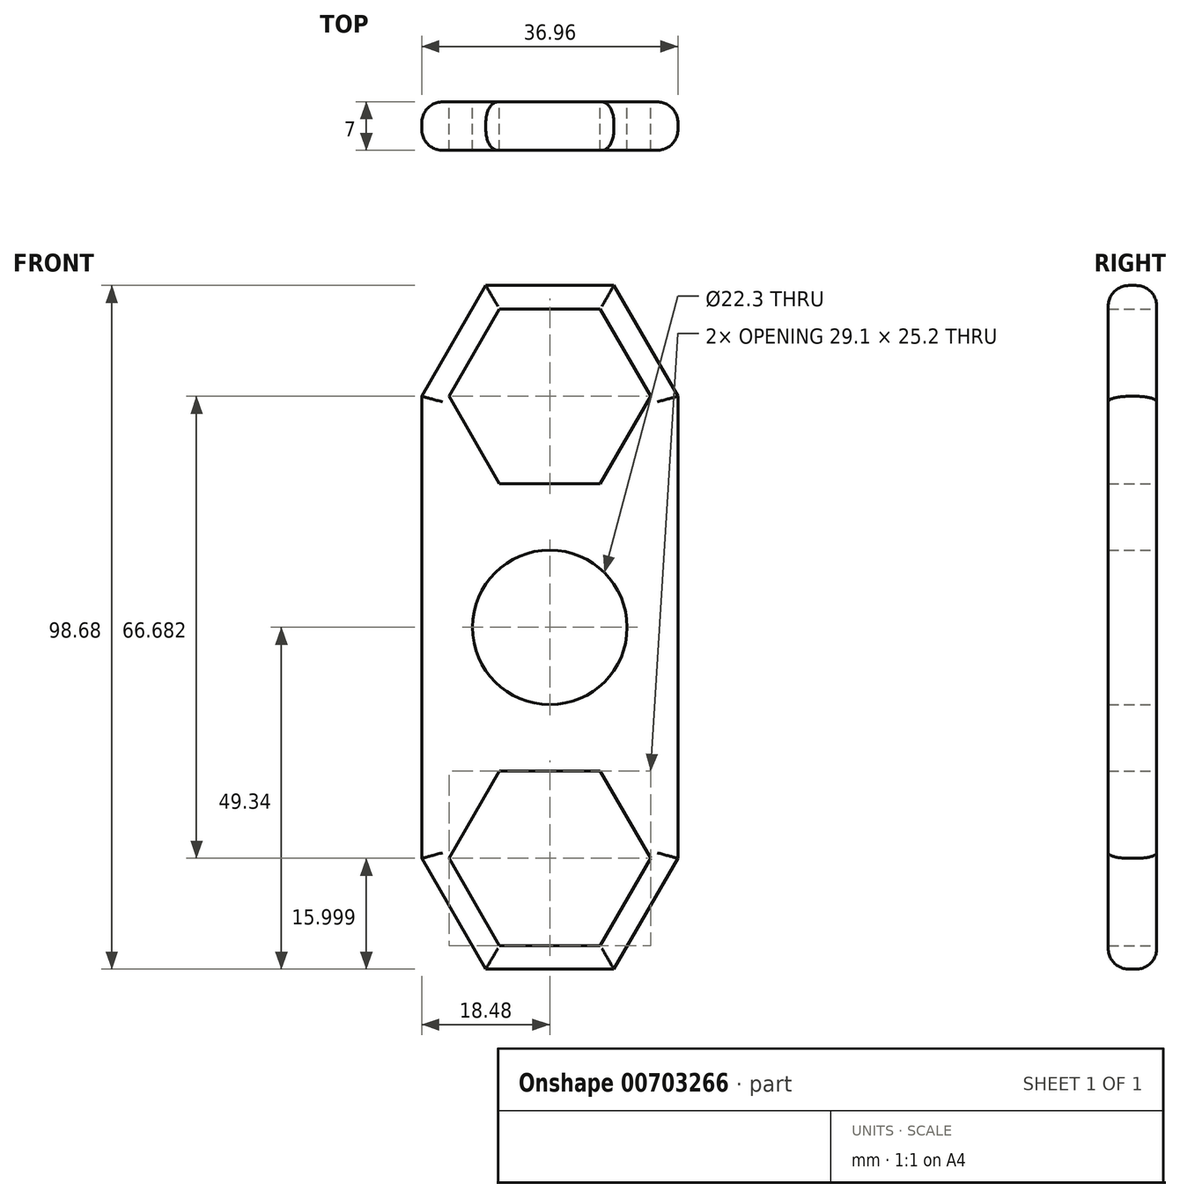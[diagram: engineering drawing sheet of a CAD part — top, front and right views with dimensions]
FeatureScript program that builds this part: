
annotation { "Feature Type Name" : "Feature", "Feature Type Description" : "" }
export const myFeature = defineFeature(function(context is Context, id is Id, definition is map)
    precondition{}
    {
        {
            var Q0;
            Q0=qCreatedBy(makeId("Front.planeOp"),FACE);
            var sketch = newSketch(context, id + "F0", { "sketchPlane" : qUnion([Q0])});
            skCircle(sketch, "E0", {"center": v(0, 0) * mm, "radius": 14.5 * mm});
            skCircle(sketch, "E1", {"center": v(0, 0) * mm, "radius": 11.15 * mm});
            skCircle(sketch, "E2.cCircle", {"center": v(0, 33.34) * mm, "radius": 12.6 * mm, "construction": true});
            skLineSegment(sketch, "E2.0", {"start": v(7.27, 20.74) * mm, "end": v(-7.27, 20.74) * mm});
            skLineSegment(sketch, "E2.1", {"start": v(-7.27, 20.74) * mm, "end": v(-14.55, 33.34) * mm});
            skLineSegment(sketch, "E2.2", {"start": v(-14.55, 33.34) * mm, "end": v(-7.27, 45.94) * mm});
            skLineSegment(sketch, "E2.3", {"start": v(-7.27, 45.94) * mm, "end": v(7.27, 45.94) * mm});
            skLineSegment(sketch, "E2.4", {"start": v(7.27, 45.94) * mm, "end": v(14.55, 33.34) * mm});
            skLineSegment(sketch, "E2.5", {"start": v(14.55, 33.34) * mm, "end": v(7.27, 20.74) * mm});
            skPoint(sketch, "E2.0.midPoint", {"position": v(0, 20.74) * mm});
            skCircle(sketch, "E3.cCircle", {"center": v(0, 33.34) * mm, "radius": 16 * mm, "construction": true});
            skLineSegment(sketch, "E3.0", {"start": v(9.24, 17.34) * mm, "end": v(-9.24, 17.34) * mm});
            skLineSegment(sketch, "E3.1", {"start": v(-9.24, 17.34) * mm, "end": v(-18.48, 33.34) * mm});
            skLineSegment(sketch, "E3.2", {"start": v(-18.48, 33.34) * mm, "end": v(-9.24, 49.34) * mm});
            skLineSegment(sketch, "E3.3", {"start": v(-9.24, 49.34) * mm, "end": v(9.24, 49.34) * mm});
            skLineSegment(sketch, "E3.4", {"start": v(9.24, 49.34) * mm, "end": v(18.48, 33.34) * mm});
            skLineSegment(sketch, "E3.5", {"start": v(18.48, 33.34) * mm, "end": v(9.24, 17.34) * mm});
            skPoint(sketch, "E3.0.midPoint", {"position": v(0, 17.34) * mm});
            skPoint(sketch, "E4.1.0", {"position": v(0, -17.34) * mm});
            skPoint(sketch, "E4.1.1", {"position": v(0, -20.74) * mm});
            skLineSegment(sketch, "E4.1.2", {"start": v(-9.24, -49.34) * mm, "end": v(-18.48, -33.34) * mm});
            skLineSegment(sketch, "E4.1.3", {"start": v(-7.27, -20.74) * mm, "end": v(7.27, -20.74) * mm});
            skLineSegment(sketch, "E4.1.4", {"start": v(-18.48, -33.34) * mm, "end": v(-9.24, -17.34) * mm});
            skLineSegment(sketch, "E4.1.5", {"start": v(9.24, -49.34) * mm, "end": v(-9.24, -49.34) * mm});
            skLineSegment(sketch, "E4.1.7", {"start": v(7.27, -45.94) * mm, "end": v(-7.27, -45.94) * mm});
            skLineSegment(sketch, "E4.1.9", {"start": v(-7.27, -45.94) * mm, "end": v(-14.55, -33.34) * mm});
            skLineSegment(sketch, "E4.1.10", {"start": v(-14.55, -33.34) * mm, "end": v(-7.27, -20.74) * mm});
            skCircle(sketch, "E4.1.11", {"center": v(0, -33.34) * mm, "radius": 16 * mm, "construction": true});
            skLineSegment(sketch, "E4.1.12", {"start": v(14.55, -33.34) * mm, "end": v(7.27, -45.94) * mm});
            skLineSegment(sketch, "E4.1.13", {"start": v(-9.24, -17.34) * mm, "end": v(9.24, -17.34) * mm});
            skCircle(sketch, "E4.1.14", {"center": v(0, -33.34) * mm, "radius": 12.6 * mm, "construction": true});
            skLineSegment(sketch, "E4.1.15", {"start": v(9.24, -17.34) * mm, "end": v(18.48, -33.34) * mm});
            skLineSegment(sketch, "E4.1.16", {"start": v(7.27, -20.74) * mm, "end": v(14.55, -33.34) * mm});
            skLineSegment(sketch, "E4.1.17", {"start": v(18.48, -33.34) * mm, "end": v(9.24, -49.34) * mm});
            skLineSegment(sketch, "E5", {"start": v(18.48, 33.34) * mm, "end": v(18.48, -33.34) * mm});
            skLineSegment(sketch, "E6", {"start": v(-18.48, 33.34) * mm, "end": v(-18.48, -33.34) * mm});
            skSolve(sketch);
        }
        {
            var Q0;
            Q0 = qSketchRegion(id + "F0", true);
            var Q1;
            Q1=makeQuery(id+"F0.imprint","IMPRINT",FACE,{"disambiguationData":[TD([[makeQuery(id+"F0.imprint","IMPRINT",EDGE,{"derivedFrom":sQuery(id+"F0.wireOp",EDGE,"E0")}),1.0]])]});
            extrude(context, id + "F1", {"entities" : qUnion([Q0, Q1]), "depth" : 7 * mm, "offsetDistance" : 25 * mm});
        }
        {
            var Q0;
            Q0=makeQuery(id+"F1.opExtrude","CAP_EDGE",EDGE,{"disambiguationData":[OSD([sQuery(id+"F0.wireOp",EDGE,"E3.2")])],"isStart":false});
            var Q1;
            Q1=makeQuery(id+"F1.opExtrude","CAP_EDGE",EDGE,{"disambiguationData":[OSD([sQuery(id+"F0.wireOp",EDGE,"E3.3")])],"isStart":false});
            var Q2;
            Q2=makeQuery(id+"F1.opExtrude","CAP_EDGE",EDGE,{"disambiguationData":[OSD([sQuery(id+"F0.wireOp",EDGE,"E3.4")])],"isStart":false});
            var Q3;
            Q3=makeQuery(id+"F1.opExtrude","CAP_EDGE",EDGE,{"disambiguationData":[OSD([sQuery(id+"F0.wireOp",EDGE,"E5")])],"isStart":false});
            var Q4;
            Q4=makeQuery(id+"F1.opExtrude","CAP_EDGE",EDGE,{"disambiguationData":[OSD([sQuery(id+"F0.wireOp",EDGE,"E6")])],"isStart":false});
            var Q5;
            Q5=makeQuery(id+"F1.opExtrude","CAP_EDGE",EDGE,{"disambiguationData":[OSD([sQuery(id+"F0.wireOp",EDGE,"E4.1.2")])],"isStart":false});
            var Q6;
            Q6=makeQuery(id+"F1.opExtrude","CAP_EDGE",EDGE,{"disambiguationData":[OSD([sQuery(id+"F0.wireOp",EDGE,"E4.1.5")])],"isStart":false});
            var Q7;
            Q7=makeQuery(id+"F1.opExtrude","CAP_EDGE",EDGE,{"disambiguationData":[OSD([sQuery(id+"F0.wireOp",EDGE,"E4.1.17")])],"isStart":false});
            var Q8;
            Q8=makeQuery(id+"F1.opExtrude","CAP_EDGE",EDGE,{"disambiguationData":[OSD([sQuery(id+"F0.wireOp",EDGE,"E4.1.5")])],"isStart":true});
            var Q9;
            Q9=makeQuery(id+"F1.opExtrude","CAP_EDGE",EDGE,{"disambiguationData":[OSD([sQuery(id+"F0.wireOp",EDGE,"E4.1.17")])],"isStart":true});
            var Q10;
            Q10=makeQuery(id+"F1.opExtrude","CAP_EDGE",EDGE,{"disambiguationData":[OSD([sQuery(id+"F0.wireOp",EDGE,"E5")])],"isStart":true});
            var Q11;
            Q11=makeQuery(id+"F1.opExtrude","CAP_EDGE",EDGE,{"disambiguationData":[OSD([sQuery(id+"F0.wireOp",EDGE,"E6")])],"isStart":true});
            var Q12;
            Q12=makeQuery(id+"F1.opExtrude","CAP_EDGE",EDGE,{"disambiguationData":[OSD([sQuery(id+"F0.wireOp",EDGE,"E3.2")])],"isStart":true});
            var Q13;
            Q13=makeQuery(id+"F1.opExtrude","CAP_EDGE",EDGE,{"disambiguationData":[OSD([sQuery(id+"F0.wireOp",EDGE,"E3.3")])],"isStart":true});
            var Q14;
            Q14=makeQuery(id+"F1.opExtrude","CAP_EDGE",EDGE,{"disambiguationData":[OSD([sQuery(id+"F0.wireOp",EDGE,"E3.4")])],"isStart":true});
            var Q15;
            Q15=makeQuery(id+"F1.opExtrude","CAP_EDGE",EDGE,{"disambiguationData":[OSD([sQuery(id+"F0.wireOp",EDGE,"E4.1.2")])],"isStart":true});
            fillet(context, id + "F2", {"entities" : qUnion([Q0, Q1, Q2, Q3, Q4, Q5, Q6, Q7, Q8, Q9, Q10, Q11, Q12, Q13, Q14, Q15]), "radius" : 3 * mm, "tangentPropagation" : true, "allowEdgeOverflow" : false});
        }
    });
